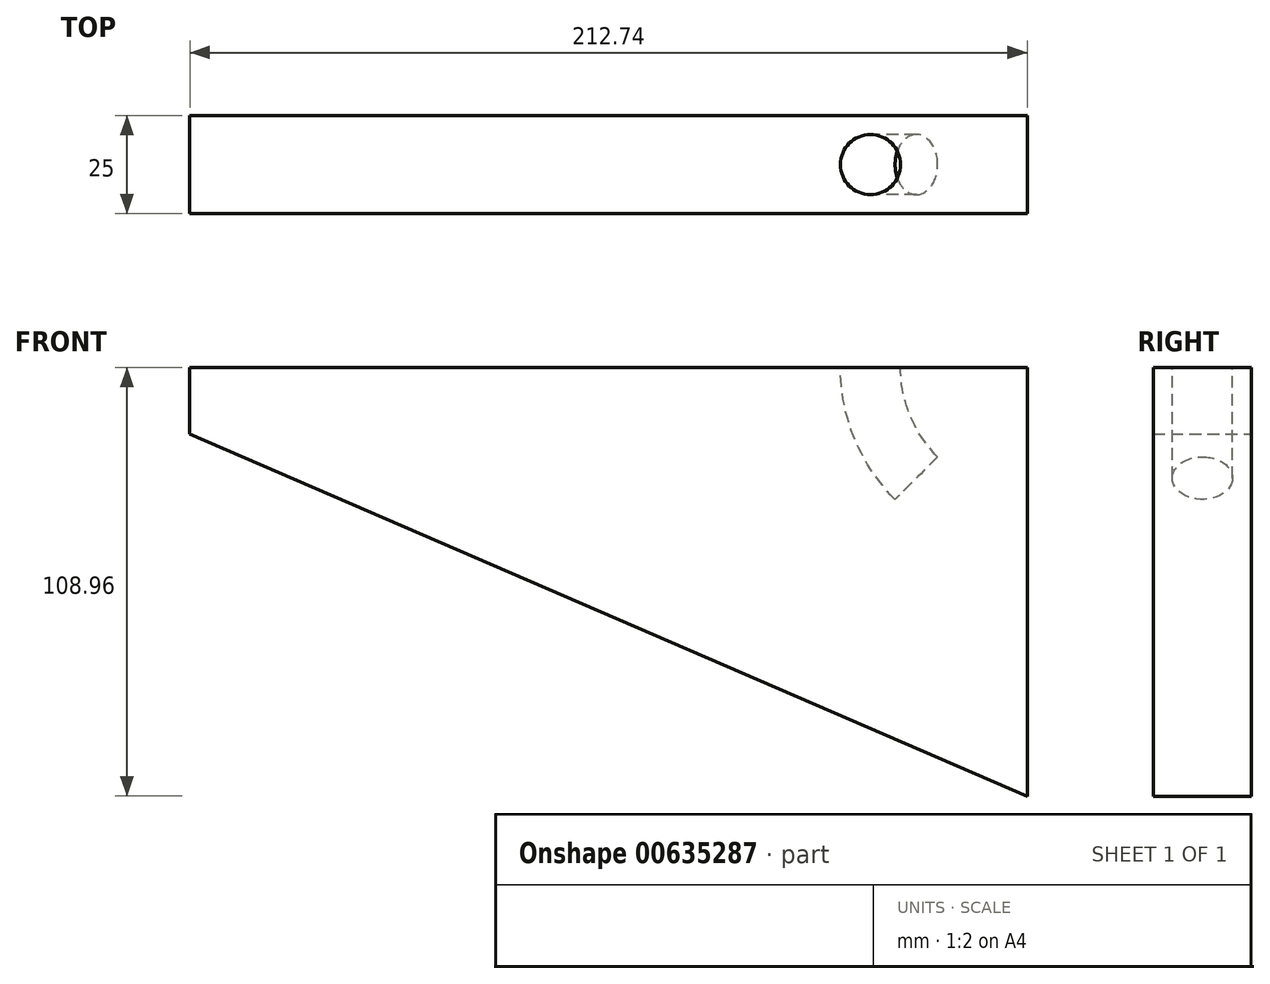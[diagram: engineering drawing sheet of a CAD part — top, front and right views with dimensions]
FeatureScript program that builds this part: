
annotation { "Feature Type Name" : "Feature", "Feature Type Description" : "" }
export const myFeature = defineFeature(function(context is Context, id is Id, definition is map)
    precondition{}
    {
        {
            var Q0;
            Q0=qCreatedBy(makeId("Front.planeOp"),FACE);
            var sketch = newSketch(context, id + "F0", { "sketchPlane" : qUnion([Q0])});
            skLineSegment(sketch, "E0.bottom", {"start": v(-98.4, 52.53) * mm, "end": v(114.34, 52.53) * mm});
            skLineSegment(sketch, "E0.top", {"start": v(-98.4, -61.65) * mm, "end": v(114.34, -61.65) * mm});
            skLineSegment(sketch, "E0.left", {"start": v(-98.4, 52.53) * mm, "end": v(-98.4, -61.65) * mm});
            skLineSegment(sketch, "E0.right", {"start": v(114.34, 52.53) * mm, "end": v(114.34, -61.65) * mm});
            skLineSegment(sketch, "E1", {"start": v(-121.18, 45.38) * mm, "end": v(128.66, -62.62) * mm});
            skSolve(sketch);
        }
        {
            var Q0;
            {var subQ0=sQuery(id+"F0.wireOp",EDGE,"E0.bottom");Q0=makeQuery(id+"F0.imprint","IMPRINT",FACE,{"disambiguationData":[TD([[makeQuery(id+"F0.imprint","IMPRINT",EDGE,{"derivedFrom":subQ0}),-1.0]])]});}
            extrude(context, id + "F1", {"entities" : qUnion([Q0]), "depth" : 25 * mm, "offsetDistance" : 25 * mm});
        }
        {
            var Q0;
            Q0=makeQuery(id+"F1.opExtrude","SWEPT_FACE",FACE,{"disambiguationData":[OSD([sQuery(id+"F0.wireOp",EDGE,"E0.bottom")])]});
            var sketch = newSketch(context, id + "F2", { "sketchPlane" : qUnion([Q0])});
            skCircle(sketch, "E2", {"center": v(74.51, -12.5) * mm, "radius": 7.64 * mm});
            skLineSegment(sketch, "E3", {"start": v(74.51, 0) * mm, "end": v(74.51, -25) * mm, "construction": true});
            skSolve(sketch);
        }
        {
            var Q0;
            Q0=makeQuery(id+"F2.imprint","IMPRINT",FACE,{"disambiguationData":[TD([[makeQuery(id+"F2.imprint","IMPRINT",EDGE,{"derivedFrom":sQuery(id+"F2.wireOp",EDGE,"E2")}),1.0]])]});
            var Q1;
            Q1=makeQuery(id+"F1.opExtrude","SWEPT_EDGE",EDGE,{"disambiguationData":[OSD([sQuery(id+"F0.wireOp",EDGE,"E0.bottom"),sQuery(id+"F0.wireOp",EDGE,"E0.right")])]});
            revolve(context, id + "F3", {"operationType" : NewBodyOperationType.REMOVE, "entities" : qUnion([Q0]), "axis" : qUnion([Q1]), "revolveType" : RevolveType.ONE_DIRECTION, "oppositeDirection" : true, "angle" : 45 * degree});
        }
    });
